FCSTD DOCUMENT  (FreeCAD 1.0R38641 +468 (Git))
Label: cad_x_axis
License: All rights reserved
LicenseURL: https://en.wikipedia.org/wiki/All_rights_reserved
objects: App::Link×3, App::Part×1
EXTERNAL_REF file=cad_x_gantry.FCStd obj=Part
EXTERNAL_REF file=k1_joint_left.FCStd obj=Part
EXTERNAL_REF file=k1_joint_right.FCStd obj=Part

FEATURE [App::Link] Link  label="x_gantry_link"
  LinkedObject = -> <external cad_x_gantry.FCStd>#Part
FEATURE [App::Link] Link001  label="joint_left_link"
  LinkPlacement = pos=(23,12.63,-2.33) rot=(0.57735,-0.57735,0.57735;2.0944rad)
  LinkedObject = -> <external k1_joint_left.FCStd>#Part
  Placement = pos=(23,12.63,-2.33) rot=(0.57735,-0.57735,0.57735;2.0944rad)
FEATURE [App::Link] Link002  label="joint_right_link"
  LinkPlacement = pos=(308.1,12.63,-2.33) rot=(0.57735,-0.57735,0.57735;2.0944rad)
  LinkedObject = -> <external k1_joint_right.FCStd>#Part
  Placement = pos=(308.1,12.63,-2.33) rot=(0.57735,-0.57735,0.57735;2.0944rad)
FEATURE [App::Part] Part  label="cad_cad_x_axis_part"
  Group = -> [Link,Link001,Link002]
  Origin = -> Origin

RESOLVED EXTERNAL PARTS (link-assembly join: the EXTERNAL_REF files above that resolve inside this repo's crawl, each included once):
---- part cad_x_gantry.FCStd = doc fcstd_a1f41f1b0959 ----
FCSTD DOCUMENT  (FreeCAD 1.0R38641 +468 (Git))
Label: cad_x_gantry
License: All rights reserved
LicenseURL: https://en.wikipedia.org/wiki/All_rights_reserved
objects: App::Link×2, App::Part×1
EXTERNAL_REF file=cad_rail_mgn9.FCStd obj=Body
EXTERNAL_REF file=cad_15x15.FCStd obj=Body

FEATURE [App::Link] Link  label="mgn9_link"
  LinkedObject = -> <external cad_rail_mgn9.FCStd>#Body
FEATURE [App::Link] Link001  label="15x15x2_link"
  LinkPlacement = pos=(30,7.5,-7.5) rot=(0.57735,0.57735,0.57735;2.0944rad)
  LinkedObject = -> <external cad_15x15.FCStd>#Body
  Placement = pos=(30,7.5,-7.5) rot=(0.57735,0.57735,0.57735;2.0944rad)
FEATURE [App::Part] Part  label="cad_x_gantry_part"
  Group = -> [Link,Link001]
  Origin = -> Origin
---- part k1_joint_left.FCStd = doc fcstd_781d79072d60 ----
FCSTD DOCUMENT  (FreeCAD 1.0R38641 +468 (Git))
Label: k1_joint_left
License: All rights reserved
LicenseURL: https://en.wikipedia.org/wiki/All_rights_reserved
objects: App::Link×5, Sketcher::SketchObject×3, PartDesign::Pocket×3, PartDesign::Pad×2, Part::Feature×1, PartDesign::FeatureBase×1, PartDesign::Body×1, App::Part×1
note: 25 computed .brp shape members not serialized (recipe doc carries the construction recipe); baked Part::Feature solids carry a one-line shape summary decoded from their .brp
EXTERNAL_REF file=cad_powge_pulley.FCStd obj=Part
EXTERNAL_REF file=cad_mgn12h_block.FCStd obj=Body
EXTERNAL_REF file=cad_M4_DIN912_30mm.FCStd obj=Body

FEATURE [Part::Feature] Part__Feature  label="step"
  shape: bbox 42.67 x 27 x 53.87 mm, 71 faces (baked)
FEATURE [PartDesign::FeatureBase] BaseFeature
  BaseFeature = -> Part__Feature
  Suppressed = false
FEATURE [App::Link] Link  label="cad_powge_pulley_top_link"
  LinkPlacement = pos=(14.8799,4.525,37.83) rot=(0,1,0;1.5708rad)
  LinkedObject = -> <external cad_powge_pulley.FCStd>#Part
  Placement = pos=(14.8799,4.525,37.83) rot=(0,1,0;1.5708rad)
FEATURE [App::Link] Link001  label="cad_powge_pulley_bottom_link"
  LinkPlacement = pos=(3.75494,18.11,24) rot=(0,1,0;1.5708rad)
  LinkedObject = -> <external cad_powge_pulley.FCStd>#Part
  Placement = pos=(3.75494,18.11,24) rot=(0,1,0;1.5708rad)
FEATURE [App::Link] Link002  label="cad_mgn12h_block_link"
  LinkPlacement = pos=(29.9999,9.5,43.2) rot=(0,1,0;1.5708rad)
  LinkedObject = -> <external cad_mgn12h_block.FCStd>#Body
  Placement = pos=(29.9999,9.5,43.2) rot=(0,1,0;1.5708rad)
FEATURE [App::Link] Link003  label="cad_m4_din912_30mm_1_link"
  LinkPlacement = pos=(-9.67,18.11,24) rot=(0,1,0;1.5708rad)
  LinkedObject = -> <external cad_M4_DIN912_30mm.FCStd>#Body
  Placement = pos=(-9.67,18.11,24) rot=(0,1,0;1.5708rad)
FEATURE [App::Link] Link004  label="cad_m4_din912_30mm_2_link"
  LinkPlacement = pos=(-5.3,4.525,37.83) rot=(0,1,0;1.5708rad)
  LinkedObject = -> <external cad_M4_DIN912_30mm.FCStd>#Body
  Placement = pos=(-5.3,4.525,37.83) rot=(0,1,0;1.5708rad)
FEATURE [Sketcher::SketchObject] Sketch
  ArcFitTolerance = 1e-06
  AttachmentSupport = -> [BaseFeature]
  ExternalGeometry = -> [BaseFeature]
  FullyConstrained = true
  MakeInternals = false
  MapMode = 5
  Placement = pos=(0,0,48) rot=(0,0,1;0rad)
  sketch-geometry (4):
    g0: LineSegment StartX=-12.67 StartY=-4 StartZ=0 EndX=-3.67 EndY=-4 EndZ=0
    g1: LineSegment StartX=-12.67 StartY=-2.8 StartZ=0 EndX=-12.67 EndY=-4 EndZ=0
    g2: LineSegment StartX=-12.67 StartY=-2.8 StartZ=0 EndX=-4.87 EndY=-2.8 EndZ=0
    g3: LineSegment StartX=-4.87 StartY=-2.8 StartZ=0 EndX=-3.67 EndY=-4 EndZ=0
  constraints (11):
    c: Coincident(g0,g-4)
    c: PointOnObject(g0,g-3)
    c: PointOnObject(g1,g-4)
    c: Coincident(g1,g0)
    c: Coincident(g2,g1)
    c: Horizontal(g2)
    c: Coincident(g3,g2)
    c: Coincident(g3,g0)
    c: Angle(g2,g3) = 2.35619
    c: Distance(g0,g0) = 9
    c: Distance(g1,g1) = 1.2
FEATURE [PartDesign::Pocket] Pocket
  BaseFeature = -> BaseFeature
  Direction = (0,0,-1)
  Length = 0
  Length2 = 5
  Profile = -> Sketch
  ReferenceAxis = -> Sketch [N_Axis]
  Refine = true
  Suppressed = false
  Type = 3
  UpToFace = -> BaseFeature [Face19]
FEATURE [PartDesign::Pad] Pad
  BaseFeature = -> Pocket
  Direction = (0,0,1)
  Length = 0.13
  Length2 = 10
  Profile = -> Pocket [Face35]
  Refine = true
  Suppressed = false
  Type = 0
FEATURE [Sketcher::SketchObject] Sketch001
  ArcFitTolerance = 1e-06
  AttachmentSupport = -> [Pad]
  ExternalGeometry = -> [Pad]
  FullyConstrained = true
  MakeInternals = false
  MapMode = 5
  Placement = pos=(0,0,19.31) rot=(1,0,0;3.14159rad)
  sketch-geometry (1):
    g0: Circle CenterX=-5.17 CenterY=-9.5 CenterZ=0 NormalX=0 NormalY=0 NormalZ=1 AngleXU=0 Radius=1.6
  constraints (2):
    c: Coincident(g0,g-3)
    c: Diameter(g0) = 3.2
FEATURE [PartDesign::Pocket] Pocket001
  BaseFeature = -> Pad
  Direction = (0,0,1)
  Length = 5
  Length2 = 5
  Profile = -> Sketch001
  ReferenceAxis = -> Sketch001 [N_Axis]
  Refine = true
  Suppressed = false
  Type = 1
FEATURE [PartDesign::Pad] Pad001
  BaseFeature = -> Pocket001
  Direction = (0,0,-1)
  Length = 5.5
  Length2 = 10
  Profile = -> Pocket001 [Face48]
  Refine = true
  Suppressed = false
  Type = 3
  UpToFace = -> Pocket001 [Face29]
FEATURE [Sketcher::SketchObject] Sketch002
  ArcFitTolerance = 1e-06
  AttachmentSupport = -> [Pad001]
  ExternalGeometry = -> [Pad001]
  FullyConstrained = true
  MakeInternals = false
  MapMode = 5
  Placement = pos=(0,0,48) rot=(0,0,1;0rad)
  sketch-geometry (1):
    g0: Circle CenterX=-5.17 CenterY=9.5 CenterZ=0 NormalX=0 NormalY=0 NormalZ=1 AngleXU=0 Radius=2.15
  constraints (2):
    c: Coincident(g0,g-3)
    c: Diameter(g0) = 4.3
FEATURE [PartDesign::Pocket] Pocket002
  BaseFeature = -> Pad001
  Direction = (0,0,-1)
  Length = 5.2
  Length2 = 5
  Profile = -> Sketch002
  ReferenceAxis = -> Sketch002 [N_Axis]
  Refine = true
  Suppressed = false
  Type = 0
FEATURE [PartDesign::Body] Body  label="k1_joint_left"
  AllowCompound = false
  BaseFeature = -> Part__Feature
  Group = -> [BaseFeature,Sketch,Pocket,Pad,Sketch001,Pocket001,Pad001,Sketch002,Pocket002]
  Origin = -> Origin
  Tip = -> Pocket002
FEATURE [App::Part] Part  label="k1_joint_left_part"
  Group = -> [Part__Feature,Body,Link,Link001,Link002,Link003,Link004]
  Origin = -> Origin001
  Placement = pos=(0,0,0) rot=(0,-1,0;1.5708rad)
---- part k1_joint_right.FCStd = doc fcstd_a37f07c89bf6 ----
FCSTD DOCUMENT  (FreeCAD 1.0R38641 +468 (Git))
Label: k1_joint_right
License: All rights reserved
LicenseURL: https://en.wikipedia.org/wiki/All_rights_reserved
objects: App::Link×5, Sketcher::SketchObject×3, PartDesign::Pocket×3, PartDesign::Pad×2, Part::Feature×1, PartDesign::FeatureBase×1, PartDesign::Body×1, App::Part×1
note: 25 computed .brp shape members not serialized (recipe doc carries the construction recipe); baked Part::Feature solids carry a one-line shape summary decoded from their .brp
EXTERNAL_REF file=cad_powge_pulley.FCStd obj=Part
EXTERNAL_REF file=cad_mgn12h_block.FCStd obj=Body
EXTERNAL_REF file=cad_M4_DIN912_30mm.FCStd obj=Body

FEATURE [Part::Feature] Part__Feature  label="step"
  shape: bbox 42.67 x 27 x 53.87 mm, 69 faces (baked)
FEATURE [PartDesign::FeatureBase] BaseFeature
  BaseFeature = -> Part__Feature
  Suppressed = false
FEATURE [App::Link] Link  label="cad_powge_pulley_top_link"
  LinkPlacement = pos=(14.85,-18.095,24) rot=(0,1,0;1.5708rad)
  LinkedObject = -> <external cad_powge_pulley.FCStd>#Part
  Placement = pos=(14.85,-18.095,24) rot=(0,1,0;1.5708rad)
FEATURE [App::Link] Link001  label="cad_powge_pulley_bottom_link"
  LinkPlacement = pos=(3.7549,-4.525,37.83) rot=(0,1,0;1.5708rad)
  LinkedObject = -> <external cad_powge_pulley.FCStd>#Part
  Placement = pos=(3.7549,-4.525,37.83) rot=(0,1,0;1.5708rad)
FEATURE [App::Link] Link002  label="cad_mgn12h_block_link"
  LinkPlacement = pos=(29.9999,-9.5,43.2) rot=(0,1,0;1.5708rad)
  LinkedObject = -> <external cad_mgn12h_block.FCStd>#Body
  Placement = pos=(29.9999,-9.5,43.2) rot=(0,1,0;1.5708rad)
FEATURE [App::Link] Link003  label="cad_m4_din912_30mm_1_link"
  LinkPlacement = pos=(-5.3,-18.095,24) rot=(0,1,0;1.5708rad)
  LinkedObject = -> <external cad_M4_DIN912_30mm.FCStd>#Body
  Placement = pos=(-5.3,-18.095,24) rot=(0,1,0;1.5708rad)
FEATURE [App::Link] Link004  label="cad_m4_din912_30mm_2_link"
  LinkPlacement = pos=(-9.67,-4.525,37.83) rot=(0,1,0;1.5708rad)
  LinkedObject = -> <external cad_M4_DIN912_30mm.FCStd>#Body
  Placement = pos=(-9.67,-4.525,37.83) rot=(0,1,0;1.5708rad)
FEATURE [Sketcher::SketchObject] Sketch
  ArcFitTolerance = 1e-06
  AttachmentSupport = -> [BaseFeature]
  ExternalGeometry = -> [BaseFeature]
  FullyConstrained = true
  MakeInternals = false
  MapMode = 5
  Placement = pos=(0,0,48) rot=(0,0,1;0rad)
  sketch-geometry (4):
    g0: LineSegment StartX=-12.67 StartY=4 StartZ=0 EndX=-3.67 EndY=4 EndZ=0
    g1: LineSegment StartX=-3.67 StartY=4 StartZ=0 EndX=-4.87 EndY=2.8 EndZ=0
    g2: LineSegment StartX=-4.87 StartY=2.8 StartZ=0 EndX=-12.67 EndY=2.8 EndZ=0
    g3: LineSegment StartX=-12.67 StartY=2.8 StartZ=0 EndX=-12.67 EndY=4 EndZ=0
  constraints (11):
    c: Coincident(g0,g-4)
    c: PointOnObject(g0,g-3)
    c: Coincident(g1,g0)
    c: Coincident(g2,g1)
    c: PointOnObject(g2,g-4)
    c: Horizontal(g2)
    c: Coincident(g3,g2)
    c: Coincident(g3,g0)
    c: Distance(g3,g3) = 1.2
    c: Distance(g0,g0) = 9
    c: Angle(g1,g2) = 2.35619
FEATURE [PartDesign::Pocket] Pocket
  BaseFeature = -> BaseFeature
  Direction = (0,0,-1)
  Length = 0
  Length2 = 5
  Profile = -> Sketch
  ReferenceAxis = -> Sketch [N_Axis]
  Refine = true
  Suppressed = false
  Type = 3
  UpToFace = -> BaseFeature [Face26]
FEATURE [PartDesign::Pad] Pad
  BaseFeature = -> Pocket
  Direction = (0,0,1)
  Length = 1.13
  Length2 = 10
  Profile = -> Pocket [Face22]
  Refine = true
  Suppressed = false
  Type = 0
FEATURE [Sketcher::SketchObject] Sketch001
  ArcFitTolerance = 1e-06
  AttachmentSupport = -> [Pad]
  ExternalGeometry = -> [Pad]
  FullyConstrained = true
  MakeInternals = false
  MapMode = 5
  Placement = pos=(0,0,19.31) rot=(1,0,0;3.14159rad)
  sketch-geometry (1):
    g0: Circle CenterX=-5.17 CenterY=9.5 CenterZ=0 NormalX=0 NormalY=0 NormalZ=1 AngleXU=0 Radius=1.6
  constraints (2):
    c: Coincident(g0,g-3)
    c: Diameter(g0) = 3.2
FEATURE [PartDesign::Pocket] Pocket001
  BaseFeature = -> Pad
  Direction = (0,0,1)
  Length = 5
  Length2 = 5
  Profile = -> Sketch001
  ReferenceAxis = -> Sketch001 [N_Axis]
  Refine = true
  Suppressed = false
  Type = 1
FEATURE [PartDesign::Pad] Pad001
  BaseFeature = -> Pocket001
  Direction = (0,0,-1)
  Length = 10
  Length2 = 10
  Profile = -> Pocket001 [Face64]
  Refine = true
  Suppressed = false
  Type = 3
  UpToFace = -> Pocket001 [Face20]
FEATURE [Sketcher::SketchObject] Sketch002
  ArcFitTolerance = 1e-06
  AttachmentSupport = -> [Pad001]
  ExternalGeometry = -> [Pad001]
  FullyConstrained = true
  MakeInternals = false
  MapMode = 5
  Placement = pos=(0,0,48) rot=(0,0,1;0rad)
  sketch-geometry (1):
    g0: Circle CenterX=-5.17 CenterY=-9.5 CenterZ=0 NormalX=0 NormalY=0 NormalZ=1 AngleXU=0 Radius=2.15
  constraints (2):
    c: Coincident(g0,g-3)
    c: Diameter(g0) = 4.3
FEATURE [PartDesign::Pocket] Pocket002
  BaseFeature = -> Pad001
  Direction = (0,0,-1)
  Length = 5.2
  Length2 = 5
  Profile = -> Sketch002
  ReferenceAxis = -> Sketch002 [N_Axis]
  Refine = true
  Suppressed = false
  Type = 0
FEATURE [PartDesign::Body] Body  label="k1_joint_right"
  AllowCompound = false
  BaseFeature = -> Part__Feature
  Group = -> [BaseFeature,Sketch,Pocket,Pad,Sketch001,Pocket001,Pad001,Sketch002,Pocket002]
  Origin = -> Origin
  Tip = -> Pocket002
FEATURE [App::Part] Part  label="k1_joint_right_part"
  Group = -> [Part__Feature,Body,Link,Link001,Link002,Link003,Link004]
  Origin = -> Origin001
  Placement = pos=(0,0,0) rot=(0.707107,0,0.707107;3.14159rad)
